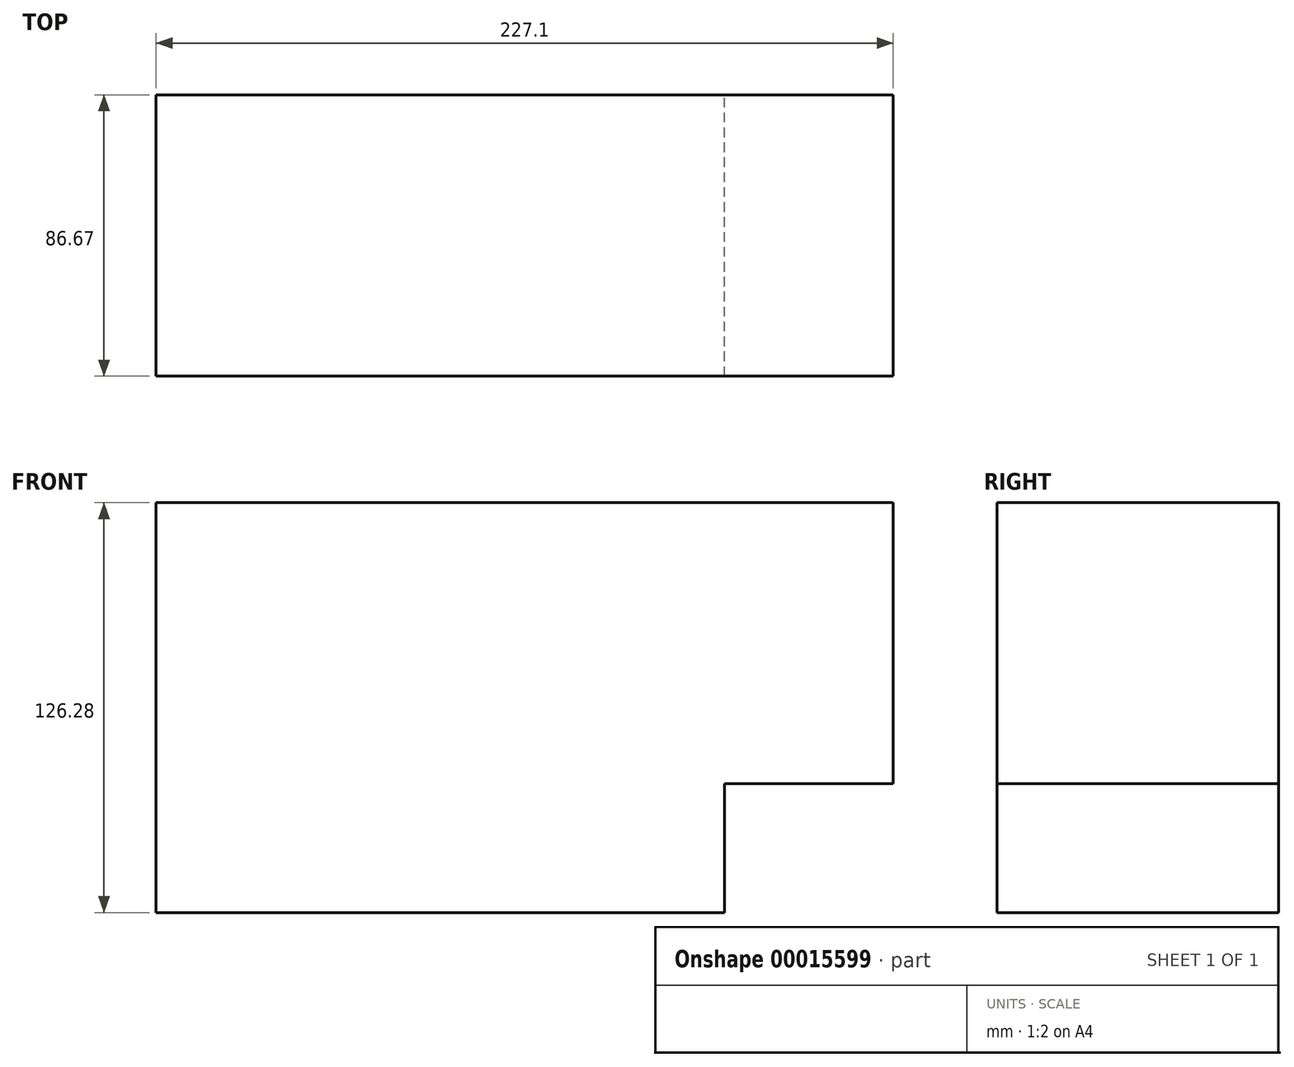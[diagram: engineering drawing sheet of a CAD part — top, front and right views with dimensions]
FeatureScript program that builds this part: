
annotation { "Feature Type Name" : "Feature", "Feature Type Description" : "" }
export const myFeature = defineFeature(function(context is Context, id is Id, definition is map)
    precondition{}
    {
        {
            var Q0;
            Q0=qCreatedBy(makeId("Front.planeOp"),FACE);
            var sketch = newSketch(context, id + "F0", { "sketchPlane" : qUnion([Q0])});
            skLineSegment(sketch, "E0.bottom", {"start": v(-109.65, 69.33) * mm, "end": v(65.44, 69.33) * mm});
            skLineSegment(sketch, "E0.top", {"start": v(-109.65, -56.95) * mm, "end": v(65.44, -56.95) * mm});
            skLineSegment(sketch, "E0.left", {"start": v(-109.65, 69.33) * mm, "end": v(-109.65, -56.95) * mm});
            skLineSegment(sketch, "E0.right", {"start": v(65.44, 69.33) * mm, "end": v(65.44, -56.95) * mm});
            skLineSegment(sketch, "E1.bottom", {"start": v(65.44, 69.33) * mm, "end": v(117.45, 69.33) * mm});
            skLineSegment(sketch, "E1.top", {"start": v(65.44, -17.24) * mm, "end": v(117.45, -17.24) * mm});
            skLineSegment(sketch, "E1.left", {"start": v(65.44, 69.33) * mm, "end": v(65.44, -17.24) * mm});
            skLineSegment(sketch, "E1.right", {"start": v(117.45, 69.33) * mm, "end": v(117.45, -17.24) * mm});
            skSolve(sketch);
        }
        {
            var Q0;
            Q0=makeQuery(id+"F0.imprint","IMPRINT",FACE,{"disambiguationData":[TD([[makeQuery(id+"F0.imprint","IMPRINT",EDGE,{"derivedFrom":sQuery(id+"F0.wireOp",EDGE,"E0.bottom")}),-1.0]])]});
            var Q1;
            Q1=makeQuery(id+"F0.imprint","IMPRINT",FACE,{"disambiguationData":[TD([[makeQuery(id+"F0.imprint","IMPRINT",EDGE,{"derivedFrom":sQuery(id+"F0.wireOp",EDGE,"E1.bottom")}),-1.0]])]});
            extrude(context, id + "F1", {"entities" : qUnion([Q0, Q1]), "depth" : 86.67 * mm});
        }
    });
